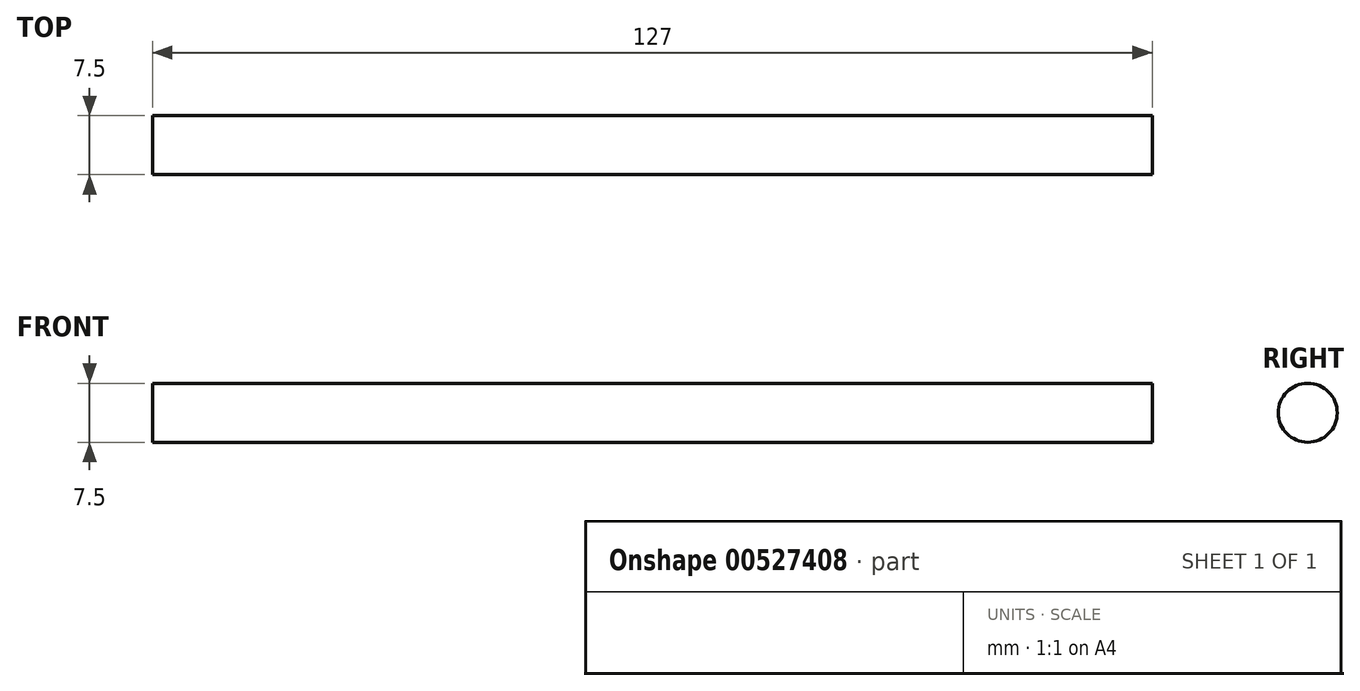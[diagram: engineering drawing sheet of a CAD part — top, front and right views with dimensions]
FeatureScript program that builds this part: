
annotation { "Feature Type Name" : "Feature", "Feature Type Description" : "" }
export const myFeature = defineFeature(function(context is Context, id is Id, definition is map)
    precondition{}
    {
        {
            var Q0;
            Q0=qCreatedBy(makeId("Right.planeOp"),FACE);
            var sketch = newSketch(context, id + "F0", { "sketchPlane" : qUnion([Q0])});
            skCircle(sketch, "E0", {"center": v(0, 0) * mm, "radius": 3.75 * mm});
            skSolve(sketch);
        }
        {
            var Q0;
            Q0 = qSketchRegion(id + "F0", true);
            extrude(context, id + "F1", {"entities" : qUnion([Q0]), "depth" : 127 * mm, "offsetDistance" : 25.4 * mm});
        }
    });
